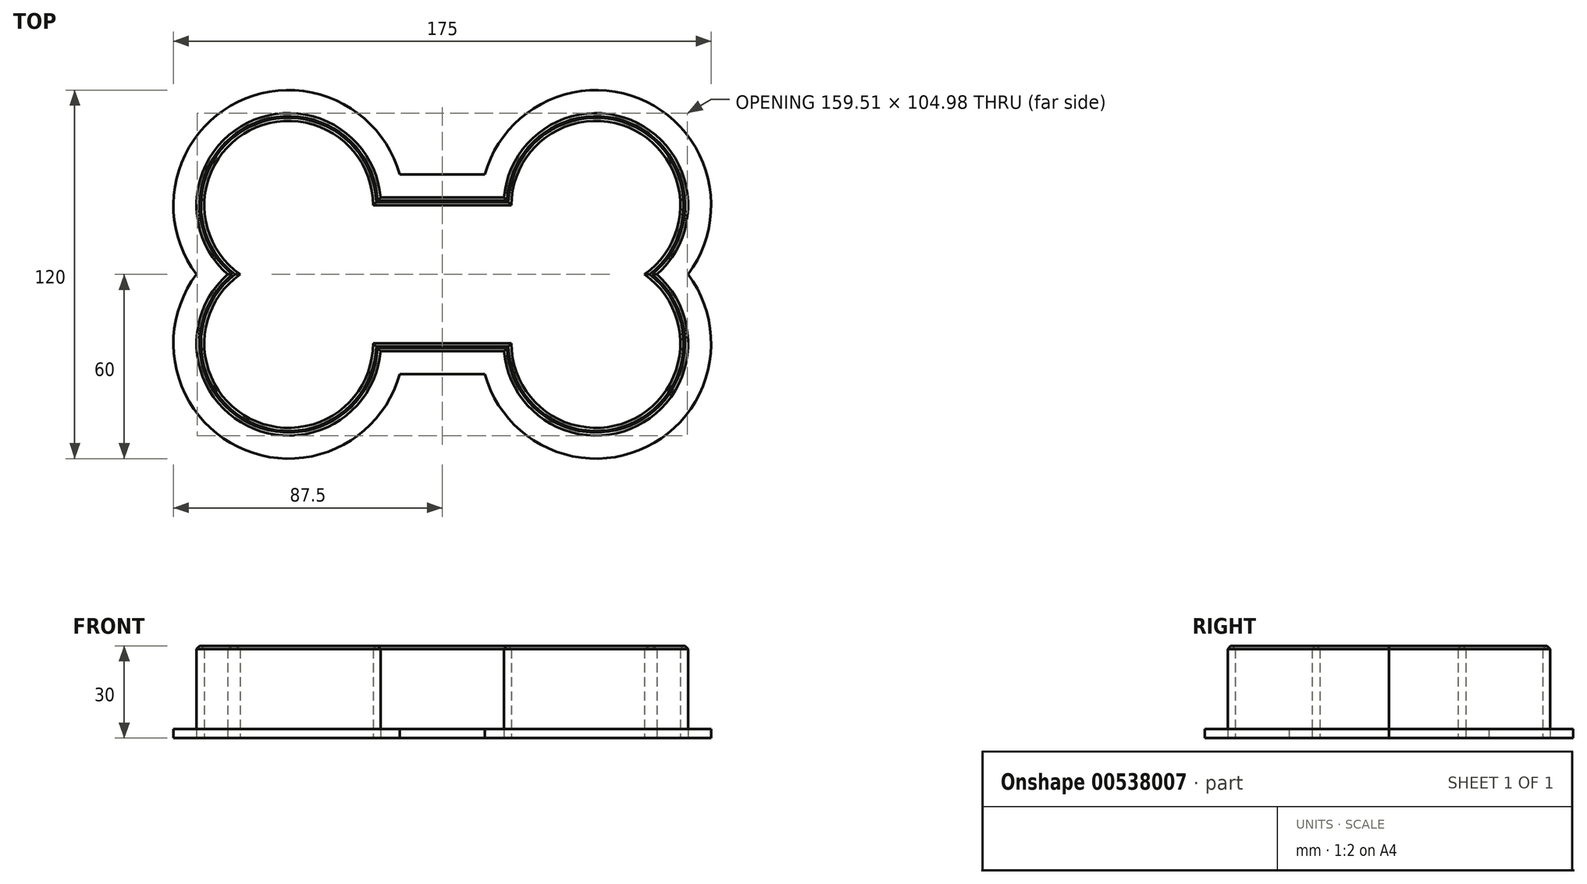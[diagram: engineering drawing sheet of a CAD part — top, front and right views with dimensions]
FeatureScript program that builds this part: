
annotation { "Feature Type Name" : "Feature", "Feature Type Description" : "" }
export const myFeature = defineFeature(function(context is Context, id is Id, definition is map)
    precondition{}
    {
        {
            var Q0;
            Q0=qCreatedBy(makeId("Top.planeOp"),FACE);
            var sketch = newSketch(context, id + "F0", { "sketchPlane" : qUnion([Q0])});
            skLineSegment(sketch, "E0.bottom", {"start": v(-50, 22.5) * mm, "end": v(-22.5, 22.5) * mm, "construction": true});
            skLineSegment(sketch, "E0.top", {"start": v(-50, -22.5) * mm, "end": v(-22.5, -22.5) * mm, "construction": true});
            skLineSegment(sketch, "E0.left", {"start": v(-50, 22.5) * mm, "end": v(-50, -22.5) * mm, "construction": true});
            skLineSegment(sketch, "E0.right", {"start": v(50, 22.5) * mm, "end": v(50, -22.5) * mm, "construction": true});
            skPoint(sketch, "E0.middle", {"position": v(0, 0) * mm});
            skArc(sketch, "E1", {"start": v(-65.81, 0) * mm, "mid": v(-62.68, -46.9) * mm, "end": v(-22.5, -22.5) * mm});
            skArc(sketch, "E2", {"start": v(-34.19, 0) * mm, "mid": v(-50, 5) * mm, "end": v(-65.81, 0) * mm, "construction": true});
            skLineSegment(sketch, "E3", {"start": v(-22.5, 22.5) * mm, "end": v(-22.5, 22.5) * mm});
            skArc(sketch, "E4", {"start": v(-22.5, -22.5) * mm, "mid": v(-25.6, -9.82) * mm, "end": v(-34.19, 0) * mm, "construction": true});
            skArc(sketch, "E5", {"start": v(34.19, 0) * mm, "mid": v(25.6, -9.82) * mm, "end": v(22.5, -22.5) * mm, "construction": true});
            skArc(sketch, "E6", {"start": v(65.81, 0) * mm, "mid": v(50, 5) * mm, "end": v(34.19, 0) * mm, "construction": true});
            skArc(sketch, "E7", {"start": v(22.5, -22.5) * mm, "mid": v(62.68, -46.9) * mm, "end": v(65.81, 0) * mm});
            skLineSegment(sketch, "E8", {"start": v(22.5, 22.5) * mm, "end": v(50, 22.5) * mm, "construction": true});
            skArc(sketch, "E9", {"start": v(-65.81, 0) * mm, "mid": v(-50, -5) * mm, "end": v(-34.19, 0) * mm, "construction": true});
            skArc(sketch, "E10", {"start": v(-34.19, 0) * mm, "mid": v(-25.6, 9.82) * mm, "end": v(-22.5, 22.5) * mm, "construction": true});
            skLineSegment(sketch, "E11", {"start": v(-22.5, 22.5) * mm, "end": v(22.5, 22.5) * mm});
            skLineSegment(sketch, "E12", {"start": v(-22.5, -22.5) * mm, "end": v(22.5, -22.5) * mm});
            skLineSegment(sketch, "E13", {"start": v(22.5, -22.5) * mm, "end": v(50, -22.5) * mm, "construction": true});
            skArc(sketch, "E14", {"start": v(-22.5, 22.5) * mm, "mid": v(-62.68, 46.9) * mm, "end": v(-65.81, 0) * mm});
            skArc(sketch, "E15", {"start": v(22.5, 22.5) * mm, "mid": v(37.32, -1.9) * mm, "end": v(65.81, 0) * mm, "construction": true});
            skArc(sketch, "E16", {"start": v(65.81, 0) * mm, "mid": v(62.68, 46.9) * mm, "end": v(22.5, 22.5) * mm});
            skLineSegment(sketch, "E17.0", {"start": v(-20.1, 25) * mm, "end": v(20.1, 25) * mm});
            skArc(sketch, "E17.1", {"start": v(-69.84, 0) * mm, "mid": v(-63.47, -49.3) * mm, "end": v(-20.1, -25) * mm});
            skLineSegment(sketch, "E17.2", {"start": v(-20.1, -25) * mm, "end": v(20.1, -25) * mm});
            skArc(sketch, "E17.3", {"start": v(-20.1, 25) * mm, "mid": v(-63.47, 49.3) * mm, "end": v(-69.84, 0) * mm});
            skArc(sketch, "E17.4", {"start": v(20.1, -25) * mm, "mid": v(63.47, -49.3) * mm, "end": v(69.84, 0) * mm});
            skArc(sketch, "E17.5", {"start": v(69.84, 0) * mm, "mid": v(63.47, 49.3) * mm, "end": v(20.1, 25) * mm});
            skLineSegment(sketch, "E18.0", {"start": v(-13.86, 32.5) * mm, "end": v(13.86, 32.5) * mm});
            skArc(sketch, "E18.1", {"start": v(-80, 0) * mm, "mid": v(-66.54, -56.16) * mm, "end": v(-13.86, -32.5) * mm});
            skLineSegment(sketch, "E18.2", {"start": v(-13.86, -32.5) * mm, "end": v(13.86, -32.5) * mm});
            skArc(sketch, "E18.3", {"start": v(-13.86, 32.5) * mm, "mid": v(-66.54, 56.16) * mm, "end": v(-80, 0) * mm});
            skArc(sketch, "E18.4", {"start": v(13.86, -32.5) * mm, "mid": v(66.54, -56.16) * mm, "end": v(80, 0) * mm});
            skArc(sketch, "E18.5", {"start": v(80, 0) * mm, "mid": v(66.54, 56.16) * mm, "end": v(13.86, 32.5) * mm});
            skSolve(sketch);
        }
        {
            var Q0;
            Q0=makeQuery(id+"F0.imprint","IMPRINT",FACE,{"disambiguationData":[TD([[makeQuery(id+"F0.imprint","IMPRINT",EDGE,{"derivedFrom":sQuery(id+"F0.wireOp",EDGE,"E17.0")}),1.0]])]});
            extrude(context, id + "F1", {"entities" : qUnion([Q0]), "depth" : 3 * mm, "offsetDistance" : 25 * mm});
        }
        {
            var Q0;
            Q0=makeQuery(id+"F0.imprint","IMPRINT",FACE,{"disambiguationData":[TD([[makeQuery(id+"F0.imprint","IMPRINT",EDGE,{"derivedFrom":sQuery(id+"F0.wireOp",EDGE,"E1")}),-1.0]])]});
            extrude(context, id + "F2", {"entities" : qUnion([Q0]), "depth" : 30 * mm, "offsetDistance" : 25 * mm});
        }
        {
            var Q0;
            Q0=makeQuery(id+"F2.opExtrude","CAP_EDGE",EDGE,{"disambiguationData":[OSD([sQuery(id+"F0.wireOp",EDGE,"E17.1")])],"isStart":false});
            var Q1;
            Q1=makeQuery(id+"F2.opExtrude","CAP_EDGE",EDGE,{"disambiguationData":[OSD([sQuery(id+"F0.wireOp",EDGE,"E17.2")])],"isStart":false});
            var Q2;
            Q2=makeQuery(id+"F2.opExtrude","CAP_EDGE",EDGE,{"disambiguationData":[OSD([sQuery(id+"F0.wireOp",EDGE,"E17.4")])],"isStart":false});
            var Q3;
            Q3=makeQuery(id+"F2.opExtrude","CAP_EDGE",EDGE,{"disambiguationData":[OSD([sQuery(id+"F0.wireOp",EDGE,"E17.5")])],"isStart":false});
            var Q4;
            Q4=makeQuery(id+"F2.opExtrude","CAP_EDGE",EDGE,{"disambiguationData":[OSD([sQuery(id+"F0.wireOp",EDGE,"E17.0")])],"isStart":false});
            var Q5;
            Q5=makeQuery(id+"F2.opExtrude","CAP_EDGE",EDGE,{"disambiguationData":[OSD([sQuery(id+"F0.wireOp",EDGE,"E17.3")])],"isStart":false});
            var Q6;
            Q6=makeQuery(id+"F2.opExtrude","CAP_EDGE",EDGE,{"disambiguationData":[OSD([sQuery(id+"F0.wireOp",EDGE,"E14")])],"isStart":false});
            var Q7;
            Q7=makeQuery(id+"F2.opExtrude","CAP_EDGE",EDGE,{"disambiguationData":[OSD([sQuery(id+"F0.wireOp",EDGE,"E1")])],"isStart":false});
            var Q8;
            Q8=makeQuery(id+"F2.opExtrude","CAP_EDGE",EDGE,{"disambiguationData":[OSD([sQuery(id+"F0.wireOp",EDGE,"E12")])],"isStart":false});
            var Q9;
            Q9=makeQuery(id+"F2.opExtrude","CAP_EDGE",EDGE,{"disambiguationData":[OSD([sQuery(id+"F0.wireOp",EDGE,"E11")])],"isStart":false});
            var Q10;
            Q10=makeQuery(id+"F2.opExtrude","CAP_EDGE",EDGE,{"disambiguationData":[OSD([sQuery(id+"F0.wireOp",EDGE,"E16")])],"isStart":false});
            var Q11;
            Q11=makeQuery(id+"F2.opExtrude","CAP_EDGE",EDGE,{"disambiguationData":[OSD([sQuery(id+"F0.wireOp",EDGE,"E7")])],"isStart":false});
            chamfer(context, id + "F3", {"entities" : qUnion([Q0, Q1, Q2, Q3, Q4, Q5, Q6, Q7, Q8, Q9, Q10, Q11]), "width" : 1 * mm, "tangentPropagation" : true});
        }
    });
